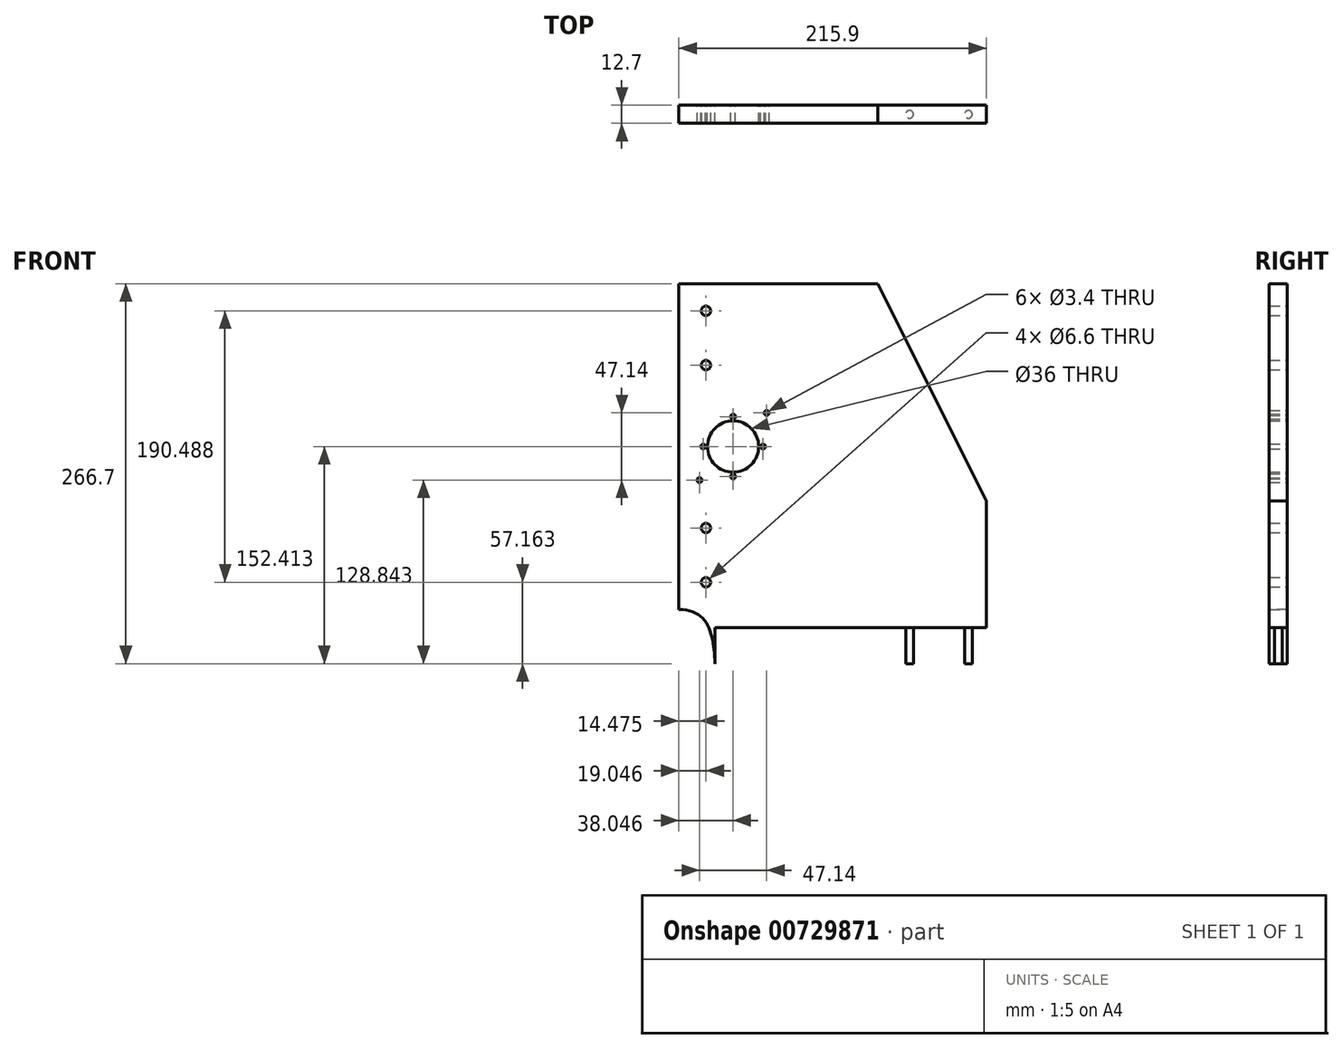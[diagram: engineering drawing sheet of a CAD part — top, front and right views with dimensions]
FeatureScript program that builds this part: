
annotation { "Feature Type Name" : "Feature", "Feature Type Description" : "" }
export const myFeature = defineFeature(function(context is Context, id is Id, definition is map)
    precondition{}
    {
        {
            var Q0;
            Q0=qCreatedBy(makeId("Front.planeOp"),FACE);
            var sketch = newSketch(context, id + "F0", { "sketchPlane" : qUnion([Q0])});
            skLineSegment(sketch, "E0.bottom", {"start": v(108.43, 152.4) * mm, "end": v(-107.47, 152.4) * mm});
            skLineSegment(sketch, "E0.left", {"start": v(108.43, 152.4) * mm, "end": v(108.43, -114.3) * mm});
            skLineSegment(sketch, "E0.right", {"start": v(-107.47, 152.4) * mm, "end": v(-107.47, -114.3) * mm});
            skPoint(sketch, "E0.middle", {"position": v(0, 0) * mm});
            skFitSpline(sketch, "E1", {"points": [v(-82.07, -114.3) * mm, v(-107.47, -76.2) * mm], "startDerivative": vector(-2.44, 55.55) * mm, "endDerivative": vector(-66.16, -0.04) * mm});
            skCircle(sketch, "E2", {"center": v(-88.42, -57.14) * mm, "radius": 3.3 * mm});
            skCircle(sketch, "E3", {"center": v(-88.42, -19.04) * mm, "radius": 3.3 * mm});
            skCircle(sketch, "E4", {"center": v(-88.42, 95.25) * mm, "radius": 3.3 * mm});
            skCircle(sketch, "E5", {"center": v(-88.42, 133.35) * mm, "radius": 3.3 * mm});
            skLineSegment(sketch, "E6", {"start": v(32.23, 152.4) * mm, "end": v(108.43, 0) * mm});
            skLineSegment(sketch, "E7", {"start": v(-107.47, -114.3) * mm, "end": v(108.43, -114.3) * mm});
            skLineSegment(sketch, "E8", {"start": v(-107.47, -76.2) * mm, "end": v(108.43, -76.2) * mm, "construction": true});
            skPoint(sketch, "E9.middle", {"position": v(-69.42, 38.11) * mm});
            skLineSegment(sketch, "E10", {"start": v(-69.42, 74.31) * mm, "end": v(-69.42, 11.11) * mm, "construction": true});
            skPoint(sketch, "E11.startSnap0", {"position": v(0.48, 152.4) * mm});
            skCircle(sketch, "E12", {"center": v(-69.42, 38.11) * mm, "radius": 18 * mm});
            skLineSegment(sketch, "E13", {"start": v(-98.77, 38.11) * mm, "end": v(-40.23, 38.11) * mm, "construction": true});
            skLineSegment(sketch, "E14", {"start": v(-91.1, 59.79) * mm, "end": v(-42.84, 11.53) * mm, "construction": true});
            skLineSegment(sketch, "E15", {"start": v(-49.22, 58.32) * mm, "end": v(-94.15, 13.39) * mm, "construction": true});
            skCircle(sketch, "E16", {"center": v(-93, 61.68) * mm, "radius": 1.7 * mm});
            skCircle(sketch, "E17.MirrorC", {"center": v(-93, 14.54) * mm, "radius": 1.7 * mm});
            skCircle(sketch, "E18.MirrorC", {"center": v(-45.85, 61.68) * mm, "radius": 1.7 * mm});
            skCircle(sketch, "E19.MirrorC", {"center": v(-45.85, 14.54) * mm, "radius": 1.7 * mm});
            skCircle(sketch, "E20", {"center": v(-69.42, 59.11) * mm, "radius": 1.7 * mm});
            skCircle(sketch, "E21.MirrorC", {"center": v(-69.42, 17.11) * mm, "radius": 1.7 * mm});
            skCircle(sketch, "E22", {"center": v(-90.42, 38.11) * mm, "radius": 1.7 * mm});
            skCircle(sketch, "E23.MirrorC", {"center": v(-48.42, 38.11) * mm, "radius": 1.7 * mm});
            skSolve(sketch);
        }
        {
            var Q0;
            {var subQ4=sQuery(id+"F0.wireOp",EDGE,"E1");Q0=makeQuery(id+"F0.imprint","IMPRINT",FACE,{"disambiguationData":[TD([[makeQuery(id+"F0.imprint","IMPRINT",EDGE,{"derivedFrom":subQ4}),-1.0]])]});}
            var Q1;
            Q1=makeQuery(id+"F0.imprint","IMPRINT",FACE,{"disambiguationData":[TD([[makeQuery(id+"F0.imprint","IMPRINT",EDGE,{"derivedFrom":sQuery(id+"F0.wireOp",EDGE,"d9uKs3Fb-to5y-7iI0-MEgy-WaLWoKfOPdlC")}),-1.0]])]});
            extrude(context, id + "F1", {"entities" : qUnion([Q0, Q1]), "depth" : 12.7 * mm, "offsetDistance" : 25.4 * mm});
        }
        {
            var Q0;
            {var subQ3=sQuery(id+"F0.wireOp",EDGE,"E1");Q0=makeQuery(id+"F0.imprint","IMPRINT",FACE,{"disambiguationData":[TD([[makeQuery(id+"F0.imprint","IMPRINT",EDGE,{"derivedFrom":subQ3}),1.0]])]});}
            var Q1;
            {var subQ2=sQuery(id+"F0.wireOp",EDGE,"E1");Q1=makeQuery(id+"F0.imprint","IMPRINT",FACE,{"disambiguationData":[TD([[makeQuery(id+"F0.imprint","IMPRINT",EDGE,{"derivedFrom":subQ2}),-1.0]])]});}
            extrude(context, id + "F2", {"entities" : qUnion([Q0, Q1]), "operationType" : NewBodyOperationType.REMOVE, "oppositeDirection" : true, "depth" : 25.4 * mm});
        }
        {
            var Q0;
            Q0=makeQuery(id+"F1.opExtrude","CAP_FACE",FACE,{"disambiguationData":[OSD([sQuery(id+"F0.wireOp",EDGE,"E0.bottom"),sQuery(id+"F0.wireOp",EDGE,"E0.right"),sQuery(id+"F0.wireOp",EDGE,"E1"),sQuery(id+"F0.wireOp",EDGE,"E2"),sQuery(id+"F0.wireOp",EDGE,"E3"),sQuery(id+"F0.wireOp",EDGE,"E4"),sQuery(id+"F0.wireOp",EDGE,"E5"),sQuery(id+"F0.wireOp",EDGE,"d9uKs3Fb-to5y-7iI0-MEgy-WaLWoKfOPdlC"),sQuery(id+"F0.wireOp",EDGE,"E7"),sQuery(id+"F0.wireOp",EDGE,"e0d6ef33-d8aa-4546-8309-47e73400ad54"),sQuery(id+"F0.wireOp",EDGE,"393e66e5-b3d4-4e39-88e2-a3308a826969"),sQuery(id+"F0.wireOp",EDGE,"b07bbd06-5e81-4e58-9e75-7104e5b17627"),sQuery(id+"F0.wireOp",EDGE,"cba16cc1-028d-47f8-8aeb-edb4e0fb6d3a"),sQuery(id+"F0.wireOp",EDGE,"E11")])],"isStart":false});
            var sketch = newSketch(context, id + "F3", { "sketchPlane" : qUnion([Q0])});
            skSolve(sketch);
        }
        {
            var Q0;
            Q0=makeQuery(id+"F1.opExtrude","SWEPT_EDGE",EDGE,{"disambiguationData":[OSD([sQuery(id+"F0.wireOp",EDGE,"E0.right"),sQuery(id+"F0.wireOp",EDGE,"E1")])]});
            var Q1;
            Q1=makeQuery(id+"F1.opExtrude","SWEPT_EDGE",EDGE,{"disambiguationData":[OSD([sQuery(id+"F0.wireOp",EDGE,"E0.bottom"),sQuery(id+"F0.wireOp",EDGE,"E0.right")])]});
            var Q2;
            Q2=makeQuery(id+"F1.opExtrude","SWEPT_EDGE",EDGE,{"disambiguationData":[OSD([sQuery(id+"F0.wireOp",EDGE,"E0.bottom"),sQuery(id+"F0.wireOp",EDGE,"E11")])]});
            var Q3;
            Q3=makeQuery(id+"F1.opExtrude","SWEPT_EDGE",EDGE,{"disambiguationData":[OSD([sQuery(id+"F0.wireOp",EDGE,"E0.left"),sQuery(id+"F0.wireOp",EDGE,"E6")])]});
            fillet(context, id + "F4", {"entities" : qUnion([Q0, Q1, Q2, Q3]), "radius" : 6.35 * mm, "tangentPropagation" : true, "allowEdgeOverflow" : false});
        }
        {
            var Q0;
            Q0=makeQuery(id+"F3.imprint","IMPRINT",FACE,{"disambiguationData":[TD([[makeQuery(id+"F3.imprint","IMPRINT",EDGE,{"derivedFrom":makeQuery(id+"F1.opExtrude","CAP_EDGE",EDGE,{"disambiguationData":[OSD([sQuery(id+"F0.wireOp",EDGE,"E17.MirrorC")])],"isStart":false})}),-1.0]])]});
            var Q1;
            Q1=makeQuery(id+"F3.imprint","IMPRINT",FACE,{"disambiguationData":[TD([[makeQuery(id+"F3.imprint","IMPRINT",EDGE,{"derivedFrom":makeQuery(id+"F1.opExtrude","CAP_EDGE",EDGE,{"disambiguationData":[OSD([sQuery(id+"F0.wireOp",EDGE,"E19.MirrorC")])],"isStart":false})}),1.0]])]});
            var Q2;
            Q2=makeQuery(id+"F3.imprint","IMPRINT",FACE,{"disambiguationData":[TD([[makeQuery(id+"F3.imprint","IMPRINT",EDGE,{"derivedFrom":makeQuery(id+"F1.opExtrude","CAP_EDGE",EDGE,{"disambiguationData":[OSD([sQuery(id+"F0.wireOp",EDGE,"E16")])],"isStart":false})}),1.0]])]});
            var Q3;
            Q3=makeQuery(id+"F3.imprint","IMPRINT",FACE,{"disambiguationData":[TD([[makeQuery(id+"F3.imprint","IMPRINT",EDGE,{"derivedFrom":makeQuery(id+"F1.opExtrude","CAP_EDGE",EDGE,{"disambiguationData":[OSD([sQuery(id+"F0.wireOp",EDGE,"E18.MirrorC")])],"isStart":false})}),-1.0]])]});
            var Q4;
            Q4=sQuery(id+"F0.wireOp",EDGE,"E16");
            var Q5;
            Q5=sQuery(id+"F0.wireOp",EDGE,"E18.MirrorC");
            var Q6;
            Q6=sQuery(id+"F0.wireOp",EDGE,"E17.MirrorC");
            var Q7;
            Q7=sQuery(id+"F0.wireOp",EDGE,"E19.MirrorC");
            extrude(context, id + "F5", {"entities" : qUnion([Q0, Q1, Q2, Q3]), "operationType" : NewBodyOperationType.ADD, "surfaceOperationType" : NewSurfaceOperationType.ADD, "surfaceEntities" : qUnion([Q4, Q5, Q6, Q7]), "oppositeDirection" : true, "depth" : 12.7 * mm, "offsetDistance" : 25.4 * mm});
        }
        {
            var Q0;
            Q0=makeQuery(id+"F1.opExtrude","SWEPT_FACE",FACE,{"disambiguationData":[OSD([sQuery(id+"F0.wireOp",EDGE,"E7")])]});
            var sketch = newSketch(context, id + "F6", { "sketchPlane" : qUnion([Q0])});
            skPoint(sketch, "E24.endSnap0", {"position": v(13.18, 6.35) * mm});
            skCircle(sketch, "E25", {"center": v(-69.37, 6.35) * mm, "radius": 2.7 * mm});
            skCircle(sketch, "E26", {"center": v(-28.1, 6.35) * mm, "radius": 2.7 * mm});
            skCircle(sketch, "E27", {"center": v(13.18, 6.35) * mm, "radius": 2.7 * mm});
            skCircle(sketch, "E28.MirrorC", {"center": v(95.73, 6.35) * mm, "radius": 2.7 * mm});
            skCircle(sketch, "E29.MirrorC", {"center": v(54.45, 6.35) * mm, "radius": 2.7 * mm});
            skSolve(sketch);
        }
        {
            var Q0;
            Q0=makeQuery(id+"F6.imprint","IMPRINT",FACE,{"disambiguationData":[TD([[makeQuery(id+"F6.imprint","IMPRINT",EDGE,{"derivedFrom":sQuery(id+"F6.wireOp",EDGE,"E25")}),1.0]])]});
            var Q1;
            Q1=makeQuery(id+"F6.imprint","IMPRINT",FACE,{"disambiguationData":[TD([[makeQuery(id+"F6.imprint","IMPRINT",EDGE,{"derivedFrom":sQuery(id+"F6.wireOp",EDGE,"E26")}),1.0]])]});
            var Q2;
            Q2=makeQuery(id+"F6.imprint","IMPRINT",FACE,{"disambiguationData":[TD([[makeQuery(id+"F6.imprint","IMPRINT",EDGE,{"derivedFrom":sQuery(id+"F6.wireOp",EDGE,"E27")}),1.0]])]});
            var Q3;
            Q3=makeQuery(id+"F6.imprint","IMPRINT",FACE,{"disambiguationData":[TD([[makeQuery(id+"F6.imprint","IMPRINT",EDGE,{"derivedFrom":sQuery(id+"F6.wireOp",EDGE,"E29.MirrorC")}),-1.0]])]});
            var Q4;
            Q4=makeQuery(id+"F6.imprint","IMPRINT",FACE,{"disambiguationData":[TD([[makeQuery(id+"F6.imprint","IMPRINT",EDGE,{"derivedFrom":sQuery(id+"F6.wireOp",EDGE,"E28.MirrorC")}),-1.0]])]});
            extrude(context, id + "F7", {"entities" : qUnion([Q0, Q1, Q2, Q3, Q4]), "operationType" : NewBodyOperationType.REMOVE, "oppositeDirection" : true, "depth" : 25.4 * mm, "offsetDistance" : 25.4 * mm});
        }
    });
